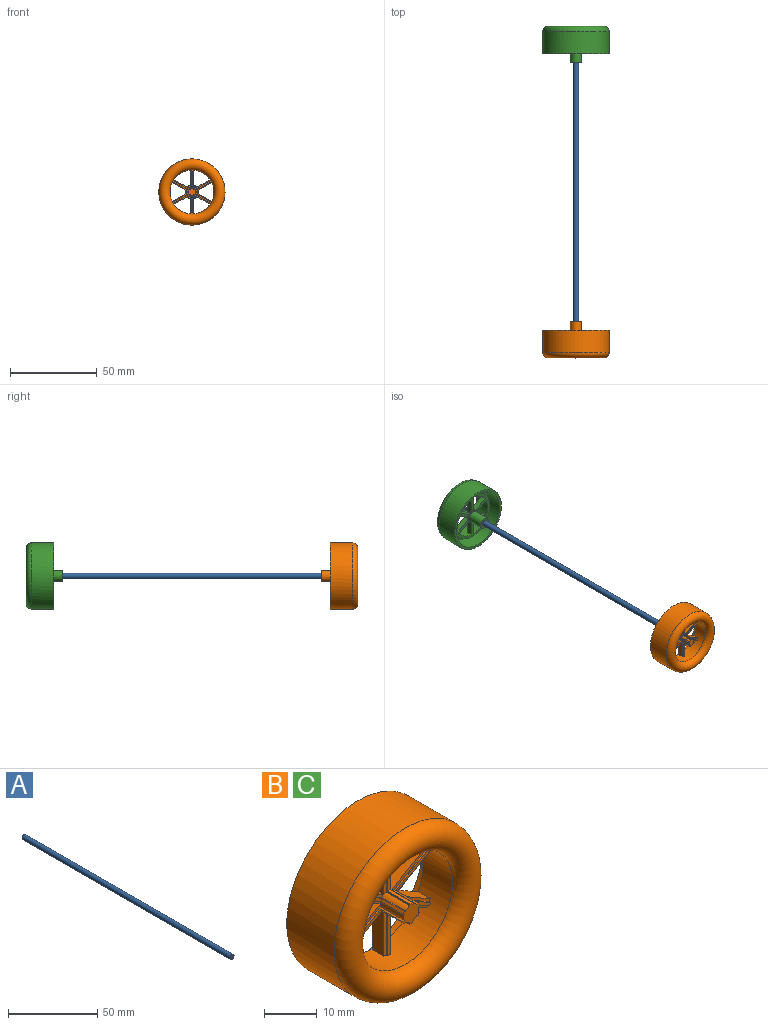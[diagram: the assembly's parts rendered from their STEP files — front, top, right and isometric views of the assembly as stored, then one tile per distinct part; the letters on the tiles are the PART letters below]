
ASSEMBLY  parts=3 mates=1
PART A: 3 faces, bbox 3.2x165.1x3.2 mm
  f0: cylinder r=1.59mm len=165.1mm, axis (0,1,0), area 1646.8mm2, adj f1,f2
  f1: plane 3.18x3.18mm, normal (0,-1,0), area 7.9mm2, adj f0
  f2: plane 3.18x3.18mm, normal (0,1,0), area 7.9mm2, adj f0
PART B: 99 faces, bbox 41.2x21x41.2 mm
  f0: plane 28.58x28.58mm, normal (0,1,0), area 234.8mm2, adj f13,f20,f21,f22,f23,f24,f25,f26
  f1: plane 38.1x38.1mm, normal (0,1,0), area 182.1mm2, adj f32,f95
  f2: cylinder r=1.98mm len=6.35mm, axis (0,1,0), area 8.8mm2, adj f3,f19,f49,f51,f71,f92
  f3: plane 9.79x5.88mm, normal (0,-1,0), area 6.6mm2, adj f2,f13,f21,f69,f92
  f4: cylinder r=1.98mm len=6.35mm, axis (0,1,0), area 8.8mm2, adj f5,f14,f48,f51,f88,f91
  f5: plane 9.58x6.01mm, normal (0,-1,0), area 6.6mm2, adj f4,f13,f23,f66,f88
  f6: cylinder r=1.98mm len=6.35mm, axis (0,1,0), area 8.8mm2, adj f7,f15,f47,f51,f84,f87
  f7: plane 10.96x0.61mm, normal (0,-1,0), area 6.6mm2, adj f6,f13,f25,f63,f84
  f8: cylinder r=1.98mm len=6.35mm, axis (0,1,0), area 8.8mm2, adj f9,f16,f46,f51,f80,f83
  f9: plane 9.79x5.88mm, normal (0,-1,0), area 6.6mm2, adj f8,f13,f27,f60,f80
  f10: plane 9.58x6.01mm, normal (0,-1,0), area 6.6mm2, adj f11,f13,f29,f57,f76
  f11: cylinder r=1.98mm len=6.35mm, axis (0,1,0), area 8.8mm2, adj f10,f17,f45,f51,f76,f79
  f12: plane 10.96x0.61mm, normal (0,-1,0), area 6.6mm2, adj f13,f31,f50,f54,f72
  f13: cylinder r=12.7mm len=25.4mm, axis (0,-1,0), area 595.4mm2, adj f0,f3,f5,f7,f9,f10,f12,f14
  f14: plane 9.58x6.01mm, normal (0,-1,0), area 6.6mm2, adj f4,f13,f22,f68,f91,f93
  f15: plane 9.79x5.88mm, normal (0,-1,0), area 6.6mm2, adj f6,f13,f24,f65,f87,f89
  f16: plane 10.96x0.61mm, normal (0,-1,0), area 6.6mm2, adj f8,f13,f26,f62,f83,f85
  f17: plane 9.58x6.01mm, normal (0,-1,0), area 6.6mm2, adj f11,f13,f28,f59,f79,f81
  f18: plane 9.79x5.88mm, normal (0,-1,0), area 6.6mm2, adj f13,f30,f50,f56,f75,f77
  f19: plane 10.96x0.61mm, normal (0,-1,0), area 6.6mm2, adj f2,f13,f20,f53,f71,f73
  f20: plane 11.01x3.18mm, normal (1,0,0), area 35mm2, adj f0,f13,f19,f21,f33,f49
  f21: plane 9.54x5.51mm, normal (-0.5,0,0.87), area 35mm2, adj f0,f3,f13,f20,f33,f49
  f22: plane 9.54x5.51mm, normal (0.5,0,-0.87), area 35mm2, adj f0,f13,f14,f23,f34,f48
  f23: plane 9.54x5.51mm, normal (0.5,0,0.87), area 35mm2, adj f0,f5,f13,f22,f34,f48
  f24: plane 9.54x5.51mm, normal (-0.5,0,-0.87), area 35mm2, adj f0,f13,f15,f25,f35,f47
  f25: plane 11.01x3.18mm, normal (1,0,0), area 35mm2, adj f0,f7,f13,f24,f35,f47
  f26: plane 11.01x3.18mm, normal (-1,0,0), area 35mm2, adj f0,f13,f16,f27,f36,f46
  f27: plane 9.54x5.51mm, normal (0.5,0,-0.87), area 35mm2, adj f0,f9,f13,f26,f36,f46
  f28: plane 9.54x5.51mm, normal (-0.5,0,0.87), area 35mm2, adj f0,f13,f17,f29,f37,f45
  f29: plane 9.54x5.51mm, normal (-0.5,0,-0.87), area 35mm2, adj f0,f10,f13,f28,f37,f45
  f30: plane 9.54x5.51mm, normal (0.5,0,0.87), area 35mm2, adj f0,f13,f18,f31,f38,f52
  f31: plane 11.01x3.18mm, normal (-1,0,0), area 35mm2, adj f0,f12,f13,f30,f38,f52
  f32: cylinder r=19.05mm len=38.1mm, axis (0,1,0), area 1520.1mm2, adj f1,f98
  f33: plane 2.2x1.91mm, normal (0,-1,0), area 2.3mm2, adj f20,f21,f39
  f34: plane 2.2x2.06mm, normal (0,-1,0), area 2.3mm2, adj f22,f23,f39
  f35: plane 2.2x1.91mm, normal (0,-1,0), area 2.3mm2, adj f24,f25,f39
  f36: plane 2.2x1.91mm, normal (0,-1,0), area 2.3mm2, adj f26,f27,f39
  f37: plane 2.2x2.06mm, normal (0,-1,0), area 2.3mm2, adj f28,f29,f39
  f38: plane 2.2x1.91mm, normal (0,-1,0), area 2.3mm2, adj f30,f31,f39
  f39: cylinder r=3.97mm len=7.94mm, axis (0,-1,0), area 9.9mm2, adj f0,f33,f34,f35,f36,f37,f38,f40
  f40: plane 7.94x7.94mm, normal (0,1,0), area 17.8mm2, adj f39,f41
  f41: cylinder r=3.17mm len=9.53mm, axis (0,-1,0), area 190mm2, adj f40,f42
  f42: plane 6.35x6.35mm, normal (0,1,0), area 23.8mm2, adj f41,f43
  f43: cylinder r=1.59mm len=7.94mm, axis (0,1,0), area 79.2mm2, adj f42,f44
  f44: plane 3.18x3.18mm, normal (0,1,0), area 7.9mm2, adj f43
  f45: plane 0.09x0.08mm, normal (0,1,0), area 0mm2, adj f11,f28,f29
  f46: plane 0.09x0.08mm, normal (0,1,0), area 0mm2, adj f8,f26,f27
  f47: plane 0.09x0.08mm, normal (0,1,0), area 0mm2, adj f6,f24,f25
  f48: plane 0.09x0.08mm, normal (0,1,0), area 0mm2, adj f4,f22,f23
  f49: plane 0.09x0.08mm, normal (0,1,0), area 0mm2, adj f2,f20,f21
  f50: cylinder r=1.98mm len=6.35mm, axis (0,1,0), area 8.8mm2, adj f12,f18,f51,f52,f72,f75
  f51: plane 4.72x4.43mm, normal (0,-1,0), area 14mm2, adj f2,f4,f6,f8,f11,f50,f71,f72
  f52: plane 0.09x0.08mm, normal (0,1,0), area 0mm2, adj f30,f31,f50
  f53: plane 10.33x0.4mm, normal (1,0,0), area 4.1mm2, adj f13,f19,f55,f73
  f54: plane 10.34x0.4mm, normal (-1,0,0), area 4.1mm2, adj f12,f13,f55,f72
  f55: plane 10.34x0.69mm, normal (0,-1,0), area 7.1mm2, adj f13,f53,f54,f74
  f56: plane 8.95x5.17mm, normal (0.5,0,0.87), area 4.1mm2, adj f13,f18,f58,f77
  f57: plane 8.95x5.17mm, normal (-0.5,0,-0.87), area 4.1mm2, adj f10,f13,f58,f76
  f58: plane 9.29x5.76mm, normal (0,-1,0), area 7.1mm2, adj f13,f56,f57,f78
  f59: plane 8.95x5.17mm, normal (-0.5,0,0.87), area 4.1mm2, adj f13,f17,f61,f81
  f60: plane 8.95x5.17mm, normal (0.5,0,-0.87), area 4.1mm2, adj f9,f13,f61,f80
  f61: plane 9.29x5.76mm, normal (0,-1,0), area 7.1mm2, adj f13,f59,f60,f82
  f62: plane 10.33x0.4mm, normal (-1,0,0), area 4.1mm2, adj f13,f16,f64,f85
  f63: plane 10.34x0.4mm, normal (1,0,0), area 4.1mm2, adj f7,f13,f64,f84
  f64: plane 10.34x0.69mm, normal (0,-1,0), area 7.1mm2, adj f13,f62,f63,f86
  f65: plane 8.95x5.17mm, normal (-0.5,0,-0.87), area 4.1mm2, adj f13,f15,f67,f89
  f66: plane 8.95x5.17mm, normal (0.5,0,0.87), area 4.1mm2, adj f5,f13,f67,f88
  f67: plane 9.29x5.76mm, normal (0,-1,0), area 7.1mm2, adj f13,f65,f66,f90
  f68: plane 8.95x5.17mm, normal (0.5,0,-0.87), area 4.1mm2, adj f13,f14,f70,f93
  f69: plane 8.95x5.17mm, normal (-0.5,0,0.87), area 4.1mm2, adj f3,f13,f70,f92
  f70: plane 9.29x5.76mm, normal (0,-1,0), area 7.1mm2, adj f13,f68,f69,f94
  f71: plane 6.35x0mm, normal (0,0,-1), area 0mm2, adj f2,f19,f51,f73
  f72: plane 6.35x0.41mm, normal (-1,0,0), area 2.6mm2, adj f12,f50,f51,f54,f74
  f73: plane 6.35x0.41mm, normal (1,0,0), area 2.6mm2, adj f19,f51,f53,f71,f74
  f74: plane 5.95x0.69mm, normal (0,0,1), area 4.1mm2, adj f51,f55,f72,f73
  f75: plane 6.35x0mm, normal (0.87,0,-0.5), area 0mm2, adj f18,f50,f51,f77
  f76: plane 6.35x0.36mm, normal (-0.5,0,-0.87), area 2.6mm2, adj f10,f11,f51,f57,f78
  f77: plane 6.35x0.36mm, normal (0.5,0,0.87), area 2.6mm2, adj f18,f51,f56,f75,f78
  f78: plane 5.95x0.6mm, normal (-0.87,0,0.5), area 4.1mm2, adj f51,f58,f76,f77
  f79: plane 6.35x0mm, normal (0.87,0,0.5), area 0mm2, adj f11,f17,f51,f81
  f80: plane 6.35x0.36mm, normal (0.5,0,-0.87), area 2.6mm2, adj f8,f9,f51,f60,f82
  f81: plane 6.35x0.36mm, normal (-0.5,0,0.87), area 2.6mm2, adj f17,f51,f59,f79,f82
  f82: plane 5.95x0.6mm, normal (-0.87,0,-0.5), area 4.1mm2, adj f51,f61,f80,f81
  f83: plane 6.35x0mm, normal (0,0,1), area 0mm2, adj f8,f16,f51,f85
  f84: plane 6.35x0.41mm, normal (1,0,0), area 2.6mm2, adj f6,f7,f51,f63,f86
  f85: plane 6.35x0.41mm, normal (-1,0,0), area 2.6mm2, adj f16,f51,f62,f83,f86
  f86: plane 5.95x0.69mm, normal (0,0,-1), area 4.1mm2, adj f51,f64,f84,f85
  f87: plane 6.35x0mm, normal (-0.87,0,0.5), area 0mm2, adj f6,f15,f51,f89
  f88: plane 6.35x0.36mm, normal (0.5,0,0.87), area 2.6mm2, adj f4,f5,f51,f66,f90
  f89: plane 6.35x0.36mm, normal (-0.5,0,-0.87), area 2.6mm2, adj f15,f51,f65,f87,f90
  f90: plane 5.95x0.6mm, normal (0.87,0,-0.5), area 4.1mm2, adj f51,f67,f88,f89
  f91: plane 6.35x0mm, normal (-0.87,0,-0.5), area 0mm2, adj f4,f14,f51,f93
  f92: plane 6.35x0.36mm, normal (-0.5,0,0.87), area 2.6mm2, adj f2,f3,f51,f69,f94
  f93: plane 6.35x0.36mm, normal (0.5,0,-0.87), area 2.6mm2, adj f14,f51,f68,f91,f94
  f94: plane 5.95x0.6mm, normal (0.87,0,0.5), area 4.1mm2, adj f51,f70,f92,f93
  f95: cylinder r=17.46mm len=34.93mm, axis (0,1,0), area 1045.1mm2, adj f1,f97
  f96: cylinder r=14.29mm len=28.58mm, axis (0,1,0), area 427.5mm2, adj f0,f97
  f97: plane 34.93x34.93mm, normal (0,1,0), area 316.7mm2, adj f95,f96
  f98: torus R=15.88mm, axis (0,-1,0), area 994.9mm2, adj f13,f32
PART C: same geometry as B
PLACE A rot(axis=(0,0,1),180deg) t=(0,-82.55,0)mm
PLACE B t=(0,-170.26,0)mm
PLACE C rot(axis=(1,0,0),180deg) t=(0,5.16,0)mm
MATE fastened A.f0 <-> B.f2  axis (0,-1,0) through (0,-165.1,0)mm
